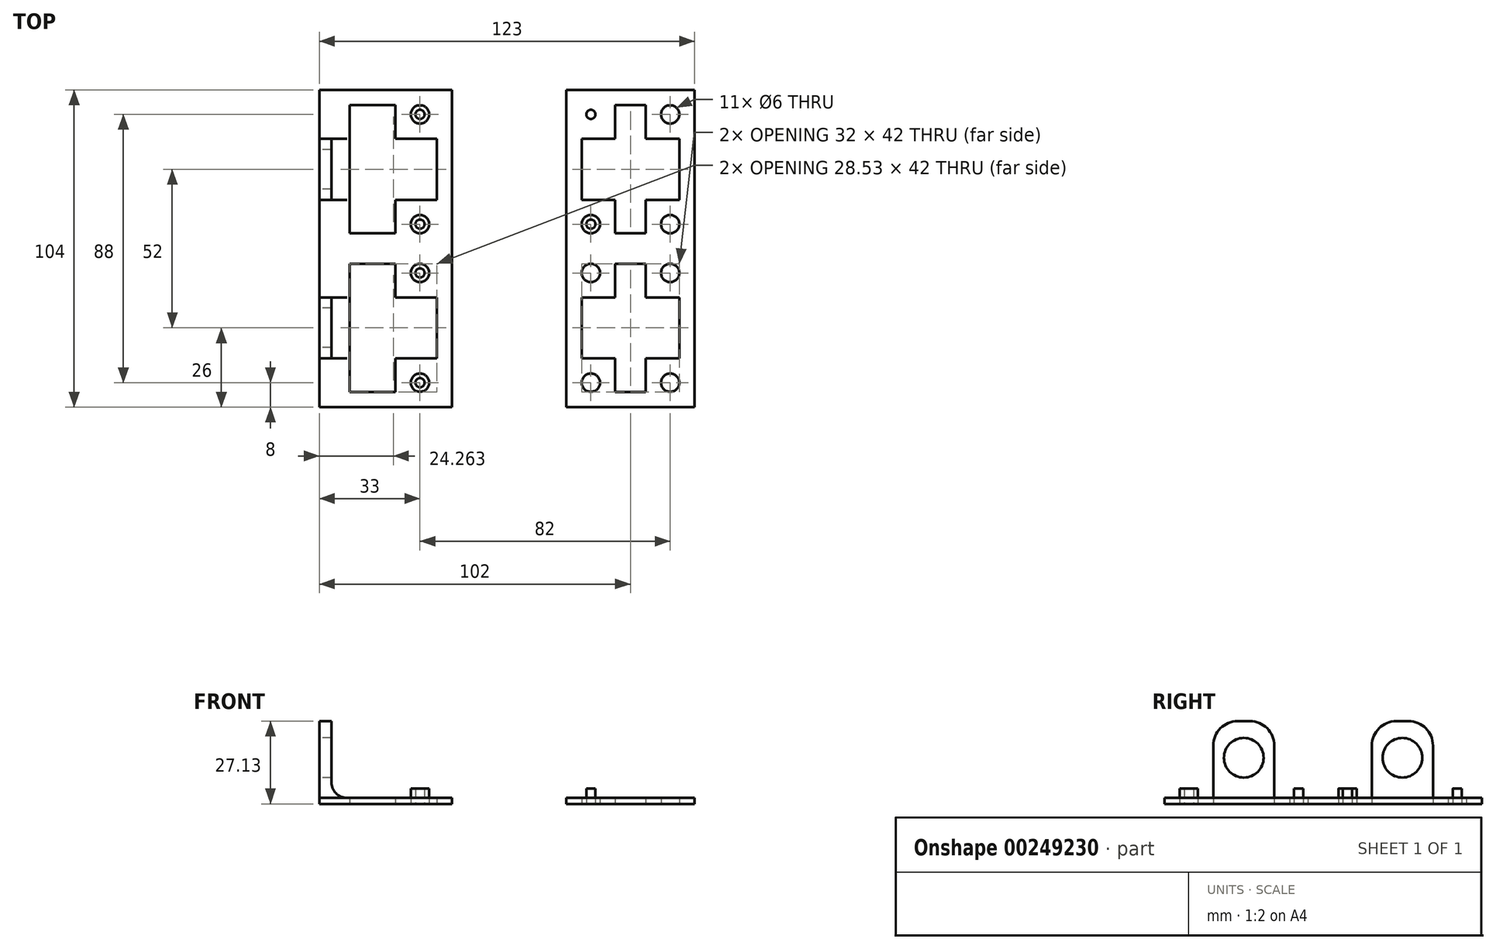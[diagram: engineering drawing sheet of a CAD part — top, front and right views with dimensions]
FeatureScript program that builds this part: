
annotation { "Feature Type Name" : "Feature", "Feature Type Description" : "" }
export const myFeature = defineFeature(function(context is Context, id is Id, definition is map)
    precondition{}
    {
        {
            var Q0;
            Q0=qCreatedBy(makeId("Top.planeOp"),FACE);
            var sketch = newSketch(context, id + "F0", { "sketchPlane" : qUnion([Q0])});
            skLineSegment(sketch, "E0.bottom", {"start": v(-10, 5) * mm, "end": v(-72, 5) * mm, "construction": true});
            skLineSegment(sketch, "E0.top", {"start": v(-10, 47) * mm, "end": v(-72, 47) * mm, "construction": true});
            skLineSegment(sketch, "E0.left", {"start": v(-10, 5) * mm, "end": v(-10, 47) * mm, "construction": true});
            skLineSegment(sketch, "E0.right", {"start": v(-72, 5) * mm, "end": v(-72, 47) * mm, "construction": true});
            skCircle(sketch, "E1", {"center": v(-13, 44) * mm, "radius": 1.5 * mm});
            skLineSegment(sketch, "E2", {"start": v(-41, 47) * mm, "end": v(-41, 5) * mm, "construction": true});
            skLineSegment(sketch, "E3", {"start": v(-72, 26) * mm, "end": v(-10, 26) * mm, "construction": true});
            skCircle(sketch, "E4.MirrorC", {"center": v(-13, 8) * mm, "radius": 1.5 * mm});
            skCircle(sketch, "E5.MirrorC", {"center": v(-69, 44) * mm, "radius": 1.5 * mm});
            skCircle(sketch, "E6.MirrorC", {"center": v(-69, 8) * mm, "radius": 1.5 * mm});
            skLineSegment(sketch, "E7", {"start": v(-102, -52) * mm, "end": v(-14, -52) * mm, "construction": true});
            skLineSegment(sketch, "E8", {"start": v(-102, 52) * mm, "end": v(-102, -52) * mm, "construction": true});
            skLineSegment(sketch, "E9", {"start": v(122, -62) * mm, "end": v(122, 62) * mm, "construction": true});
            skLineSegment(sketch, "E10.bottom", {"start": v(-102, 52) * mm, "end": v(-58.47, 52) * mm});
            skLineSegment(sketch, "E10.top", {"start": v(-102, -52) * mm, "end": v(-48, -52) * mm});
            skLineSegment(sketch, "E10.left", {"start": v(-102, 52) * mm, "end": v(-102, -52) * mm});
            skCircle(sketch, "E11", {"center": v(-13, 44) * mm, "radius": 3 * mm});
            skCircle(sketch, "E12.MirrorC", {"center": v(-13, 8) * mm, "radius": 3 * mm});
            skCircle(sketch, "E13.MirrorC", {"center": v(-69, 44) * mm, "radius": 3 * mm});
            skCircle(sketch, "E14.MirrorC", {"center": v(-69, 8) * mm, "radius": 3 * mm});
            skLineSegment(sketch, "E15", {"start": v(-58.47, 52) * mm, "end": v(-58.47, -52) * mm});
            skPoint(sketch, "E16.MirrorCS.end.orphan", {"position": v(102, -52) * mm});
            skPoint(sketch, "E16.MirrorCS.start.orphan", {"position": v(102, 52) * mm});
            skPoint(sketch, "E17.trimOffspring.end.orphan", {"position": v(48, -52) * mm});
            skLineSegment(sketch, "E18.MirrorCS", {"start": v(20, 52) * mm, "end": v(-23.53, 52) * mm});
            skLineSegment(sketch, "E19.MirrorCS", {"start": v(20, -52) * mm, "end": v(-68, -52) * mm, "construction": true});
            skLineSegment(sketch, "E20.bottom", {"start": v(-23.53, 52) * mm, "end": v(20, 52) * mm});
            skLineSegment(sketch, "E20.top", {"start": v(-24.76, -52) * mm, "end": v(20, -52) * mm});
            skCircle(sketch, "E21.MirrorC", {"center": v(13, 44) * mm, "radius": 3 * mm});
            skCircle(sketch, "E22.MirrorC", {"center": v(13, 44) * mm, "radius": 1.5 * mm});
            skCircle(sketch, "E23.MirrorC", {"center": v(13, 8) * mm, "radius": 3 * mm});
            skCircle(sketch, "E24.MirrorC", {"center": v(13, 8) * mm, "radius": 1.5 * mm});
            skLineSegment(sketch, "E25.MirrorCS", {"start": v(72, 5) * mm, "end": v(72, 47) * mm, "construction": true});
            skLineSegment(sketch, "E26.MirrorCS", {"start": v(10, 5) * mm, "end": v(10, 47) * mm, "construction": true});
            skLineSegment(sketch, "E27.MirrorCS", {"start": v(10, 5) * mm, "end": v(72, 5) * mm, "construction": true});
            skLineSegment(sketch, "E28.MirrorCS", {"start": v(10, 47) * mm, "end": v(72, 47) * mm, "construction": true});
            skLineSegment(sketch, "E29.bottom", {"start": v(-77, 47) * mm, "end": v(-92, 47) * mm});
            skLineSegment(sketch, "E29.top", {"start": v(-77, 5) * mm, "end": v(-92, 5) * mm});
            skLineSegment(sketch, "E29.left", {"start": v(-77, 47) * mm, "end": v(-77, 5) * mm});
            skLineSegment(sketch, "E29.right", {"start": v(-92, 47) * mm, "end": v(-92, 5) * mm});
            skLineSegment(sketch, "E30.bottom", {"start": v(-5, 47) * mm, "end": v(5, 47) * mm});
            skLineSegment(sketch, "E30.top", {"start": v(-5, 5) * mm, "end": v(5, 5) * mm});
            skLineSegment(sketch, "E30.left", {"start": v(-5, 47) * mm, "end": v(-5, 5) * mm});
            skLineSegment(sketch, "E30.right", {"start": v(5, 47) * mm, "end": v(5, 5) * mm});
            skCircle(sketch, "E31.MirrorC", {"center": v(-69, -8) * mm, "radius": 1.5 * mm});
            skCircle(sketch, "E32.MirrorC", {"center": v(-69, -8) * mm, "radius": 3 * mm});
            skCircle(sketch, "E33.MirrorC", {"center": v(-13, -8) * mm, "radius": 3 * mm});
            skCircle(sketch, "E34.MirrorC", {"center": v(-13, -8) * mm, "radius": 1.5 * mm});
            skCircle(sketch, "E35.MirrorC", {"center": v(13, -8) * mm, "radius": 3 * mm});
            skCircle(sketch, "E36.MirrorC", {"center": v(13, -8) * mm, "radius": 1.5 * mm});
            skCircle(sketch, "E37.MirrorC", {"center": v(13, -44) * mm, "radius": 3 * mm});
            skCircle(sketch, "E38.MirrorC", {"center": v(13, -44) * mm, "radius": 1.5 * mm});
            skCircle(sketch, "E39.MirrorC", {"center": v(-13, -44) * mm, "radius": 3 * mm});
            skCircle(sketch, "E40.MirrorC", {"center": v(-13, -44) * mm, "radius": 1.5 * mm});
            skCircle(sketch, "E41.MirrorC", {"center": v(-69, -44) * mm, "radius": 3 * mm});
            skCircle(sketch, "E42.MirrorC", {"center": v(-69, -44) * mm, "radius": 1.5 * mm});
            skLineSegment(sketch, "E43.MirrorCS", {"start": v(-10, -5) * mm, "end": v(-72, -5) * mm, "construction": true});
            skLineSegment(sketch, "E44.MirrorCS", {"start": v(-10, -47) * mm, "end": v(-72, -47) * mm, "construction": true});
            skLineSegment(sketch, "E45.MirrorCS", {"start": v(-72, -5) * mm, "end": v(-72, -47) * mm, "construction": true});
            skLineSegment(sketch, "E46.MirrorCS", {"start": v(-10, -5) * mm, "end": v(-10, -47) * mm, "construction": true});
            skLineSegment(sketch, "E47.MirrorCS", {"start": v(10, -5) * mm, "end": v(10, -47) * mm, "construction": true});
            skLineSegment(sketch, "E48.MirrorCS", {"start": v(10, -5) * mm, "end": v(72, -5) * mm, "construction": true});
            skLineSegment(sketch, "E49.MirrorCS", {"start": v(10, -47) * mm, "end": v(72, -47) * mm, "construction": true});
            skLineSegment(sketch, "E50.MirrorCS", {"start": v(72, -5) * mm, "end": v(72, -47) * mm, "construction": true});
            skLineSegment(sketch, "E51.MirrorCS", {"start": v(-92, -47) * mm, "end": v(-92, -5) * mm});
            skLineSegment(sketch, "E52.MirrorCS", {"start": v(-77, -47) * mm, "end": v(-92, -47) * mm});
            skLineSegment(sketch, "E53.MirrorCS", {"start": v(-77, -47) * mm, "end": v(-77, -5) * mm});
            skLineSegment(sketch, "E54.MirrorCS", {"start": v(-77, -5) * mm, "end": v(-92, -5) * mm});
            skLineSegment(sketch, "E55.MirrorCS", {"start": v(-5, -5) * mm, "end": v(5, -5) * mm});
            skLineSegment(sketch, "E56.MirrorCS", {"start": v(5, -47) * mm, "end": v(5, -5) * mm});
            skLineSegment(sketch, "E57.MirrorCS", {"start": v(-5, -47) * mm, "end": v(-5, -5) * mm});
            skLineSegment(sketch, "E58.MirrorCS", {"start": v(-5, -47) * mm, "end": v(5, -47) * mm});
            skLineSegment(sketch, "E59.bottom", {"start": v(-80.53, 36) * mm, "end": v(-63.47, 36) * mm});
            skLineSegment(sketch, "E59.top", {"start": v(-80.53, 16) * mm, "end": v(-63.47, 16) * mm});
            skLineSegment(sketch, "E59.left", {"start": v(-80.53, 36) * mm, "end": v(-80.53, 16) * mm});
            skLineSegment(sketch, "E59.right", {"start": v(-63.47, 36) * mm, "end": v(-63.47, 16) * mm});
            skPoint(sketch, "E59.middle", {"position": v(-72, 26) * mm});
            skLineSegment(sketch, "E60.MirrorCS", {"start": v(-63.47, -36) * mm, "end": v(-63.47, -16) * mm});
            skLineSegment(sketch, "E61.MirrorCS", {"start": v(-80.53, -16) * mm, "end": v(-63.47, -16) * mm});
            skLineSegment(sketch, "E62.MirrorCS", {"start": v(-80.53, -36) * mm, "end": v(-80.53, -16) * mm});
            skLineSegment(sketch, "E63.MirrorCS", {"start": v(-80.53, -36) * mm, "end": v(-63.47, -36) * mm});
            skLineSegment(sketch, "E64", {"start": v(-10, 26) * mm, "end": v(10, 26) * mm, "construction": true});
            skLineSegment(sketch, "E65", {"start": v(0, 47) * mm, "end": v(0, 5) * mm, "construction": true});
            skLineSegment(sketch, "E66.bottom", {"start": v(-16, 36) * mm, "end": v(16, 36) * mm});
            skLineSegment(sketch, "E66.top", {"start": v(-16, 16) * mm, "end": v(16, 16) * mm});
            skLineSegment(sketch, "E66.left", {"start": v(-16, 36) * mm, "end": v(-16, 16) * mm});
            skLineSegment(sketch, "E66.right", {"start": v(16, 36) * mm, "end": v(16, 16) * mm});
            skPoint(sketch, "E66.middle", {"position": v(0, 26) * mm});
            skLineSegment(sketch, "E67.bottom", {"start": v(20, 52) * mm, "end": v(-20, 52) * mm});
            skLineSegment(sketch, "E67.top", {"start": v(20, -52) * mm, "end": v(-20, -52) * mm});
            skPoint(sketch, "E67.middle", {"position": v(0, 0) * mm});
            skPoint(sketch, "E68.trimOffspring.end.orphan", {"position": v(-23.53, -52) * mm});
            skLineSegment(sketch, "E69.bottom", {"start": v(21, 52) * mm, "end": v(-21, 52) * mm});
            skLineSegment(sketch, "E69.top", {"start": v(21, -52) * mm, "end": v(-21, -52) * mm});
            skLineSegment(sketch, "E69.left", {"start": v(21, 52) * mm, "end": v(21, -52) * mm});
            skLineSegment(sketch, "E69.right", {"start": v(-21, 52) * mm, "end": v(-21, -52) * mm});
            skLineSegment(sketch, "E70.MirrorCS", {"start": v(16, -36) * mm, "end": v(16, -16) * mm});
            skLineSegment(sketch, "E71.MirrorCS", {"start": v(-16, -36) * mm, "end": v(16, -36) * mm});
            skLineSegment(sketch, "E72.MirrorCS", {"start": v(-16, -36) * mm, "end": v(-16, -16) * mm});
            skLineSegment(sketch, "E73.MirrorCS", {"start": v(-16, -16) * mm, "end": v(16, -16) * mm});
            skSolve(sketch);
        }
        {
            var Q0;
            Q0=makeQuery(id+"F0.imprint","IMPRINT",FACE,{"disambiguationData":[TD([[makeQuery(id+"F0.imprint","IMPRINT",EDGE,{"derivedFrom":sQuery(id+"F0.wireOp",EDGE,"E4.MirrorC")}),1.0]])]});
            var Q1;
            Q1=makeQuery(id+"F0.imprint","IMPRINT",FACE,{"disambiguationData":[TD([[makeQuery(id+"F0.imprint","IMPRINT",EDGE,{"derivedFrom":sQuery(id+"F0.wireOp",EDGE,"E10.bottom")}),-1.0]])]});
            var Q2;
            Q2=makeQuery(id+"F0.imprint","IMPRINT",FACE,{"disambiguationData":[TD([[makeQuery(id+"F0.imprint","IMPRINT",EDGE,{"derivedFrom":sQuery(id+"F0.wireOp",EDGE,"E1")}),-1.0]])]});
            var Q3;
            Q3=makeQuery(id+"F0.imprint","IMPRINT",FACE,{"disambiguationData":[TD([[makeQuery(id+"F0.imprint","IMPRINT",EDGE,{"derivedFrom":sQuery(id+"F0.wireOp",EDGE,"E4.MirrorC")}),1.0]])]});
            var Q4;
            Q4=makeQuery(id+"F0.imprint","IMPRINT",FACE,{"disambiguationData":[TD([[makeQuery(id+"F0.imprint","IMPRINT",EDGE,{"derivedFrom":sQuery(id+"F0.wireOp",EDGE,"E11")}),-1.0]])]});
            extrude(context, id + "F1", {"entities" : qUnion([Q0, Q1, Q2, Q3, Q4]), "depth" : 2 * mm});
        }
        {
            var Q0;
            Q0=makeQuery(id+"F0.imprint","IMPRINT",FACE,{"disambiguationData":[TD([[makeQuery(id+"F0.imprint","IMPRINT",EDGE,{"derivedFrom":sQuery(id+"F0.wireOp",EDGE,"E5.MirrorC")}),1.0]])]});
            var Q1;
            Q1=makeQuery(id+"F0.imprint","IMPRINT",FACE,{"disambiguationData":[TD([[makeQuery(id+"F0.imprint","IMPRINT",EDGE,{"derivedFrom":sQuery(id+"F0.wireOp",EDGE,"E6.MirrorC")}),-1.0]])]});
            var Q2;
            Q2=makeQuery(id+"F0.imprint","IMPRINT",FACE,{"disambiguationData":[TD([[makeQuery(id+"F0.imprint","IMPRINT",EDGE,{"derivedFrom":sQuery(id+"F0.wireOp",EDGE,"E4.MirrorC")}),1.0]])]});
            var Q3;
            Q3=makeQuery(id+"F0.imprint","IMPRINT",FACE,{"disambiguationData":[TD([[makeQuery(id+"F0.imprint","IMPRINT",EDGE,{"derivedFrom":sQuery(id+"F0.wireOp",EDGE,"E1")}),-1.0]])]});
            var Q4;
            Q4=makeQuery(id+"F0.imprint","IMPRINT",FACE,{"disambiguationData":[TD([[makeQuery(id+"F0.imprint","IMPRINT",EDGE,{"derivedFrom":sQuery(id+"F0.wireOp",EDGE,"54afa595-782a-44cc-b530-174a9ed369d55.MirrorC")}),1.0]])]});
            var Q5;
            Q5=makeQuery(id+"F0.imprint","IMPRINT",FACE,{"disambiguationData":[TD([[makeQuery(id+"F0.imprint","IMPRINT",EDGE,{"derivedFrom":sQuery(id+"F0.wireOp",EDGE,"54afa595-782a-44cc-b530-174a9ed369d57.MirrorC")}),-1.0]])]});
            var Q6;
            Q6=makeQuery(id+"F0.imprint","IMPRINT",FACE,{"disambiguationData":[TD([[makeQuery(id+"F0.imprint","IMPRINT",EDGE,{"derivedFrom":sQuery(id+"F0.wireOp",EDGE,"25e94151-ceff-47d8-9de0-a60d4fc2466f5.MirrorC")}),1.0]])]});
            var Q7;
            Q7=makeQuery(id+"F0.imprint","IMPRINT",FACE,{"disambiguationData":[TD([[makeQuery(id+"F0.imprint","IMPRINT",EDGE,{"derivedFrom":sQuery(id+"F0.wireOp",EDGE,"25e94151-ceff-47d8-9de0-a60d4fc2466f7.MirrorC")}),-1.0]])]});
            var Q8;
            Q8=makeQuery(id+"F0.imprint","IMPRINT",FACE,{"disambiguationData":[TD([[makeQuery(id+"F0.imprint","IMPRINT",EDGE,{"derivedFrom":sQuery(id+"F0.wireOp",EDGE,"54afa595-782a-44cc-b530-174a9ed369d59.MirrorC")}),-1.0]])]});
            var Q9;
            Q9=makeQuery(id+"F0.imprint","IMPRINT",FACE,{"disambiguationData":[TD([[makeQuery(id+"F0.imprint","IMPRINT",EDGE,{"derivedFrom":sQuery(id+"F0.wireOp",EDGE,"25e94151-ceff-47d8-9de0-a60d4fc2466f19.MirrorC")}),1.0]])]});
            var Q10;
            Q10=makeQuery(id+"F0.imprint","IMPRINT",FACE,{"disambiguationData":[TD([[makeQuery(id+"F0.imprint","IMPRINT",EDGE,{"derivedFrom":sQuery(id+"F0.wireOp",EDGE,"25e94151-ceff-47d8-9de0-a60d4fc2466f14.MirrorC")}),-1.0]])]});
            var Q11;
            Q11=makeQuery(id+"F0.imprint","IMPRINT",FACE,{"disambiguationData":[TD([[makeQuery(id+"F0.imprint","IMPRINT",EDGE,{"derivedFrom":sQuery(id+"F0.wireOp",EDGE,"25e94151-ceff-47d8-9de0-a60d4fc2466f6.MirrorC")}),-1.0]])]});
            var Q12;
            Q12=makeQuery(id+"F0.imprint","IMPRINT",FACE,{"disambiguationData":[TD([[makeQuery(id+"F0.imprint","IMPRINT",EDGE,{"derivedFrom":sQuery(id+"F0.wireOp",EDGE,"25e94151-ceff-47d8-9de0-a60d4fc2466f11.MirrorC")}),1.0]])]});
            var Q13;
            Q13=makeQuery(id+"F0.imprint","IMPRINT",FACE,{"disambiguationData":[TD([[makeQuery(id+"F0.imprint","IMPRINT",EDGE,{"derivedFrom":sQuery(id+"F0.wireOp",EDGE,"25e94151-ceff-47d8-9de0-a60d4fc2466f16.MirrorC")}),1.0]])]});
            var Q14;
            Q14=makeQuery(id+"F0.imprint","IMPRINT",FACE,{"disambiguationData":[TD([[makeQuery(id+"F0.imprint","IMPRINT",EDGE,{"derivedFrom":sQuery(id+"F0.wireOp",EDGE,"54afa595-782a-44cc-b530-174a9ed369d53.MirrorC")}),1.0]])]});
            var Q15;
            Q15=makeQuery(id+"F0.imprint","IMPRINT",FACE,{"disambiguationData":[TD([[makeQuery(id+"F0.imprint","IMPRINT",EDGE,{"derivedFrom":sQuery(id+"F0.wireOp",EDGE,"25e94151-ceff-47d8-9de0-a60d4fc2466f17.MirrorC")}),-1.0]])]});
            var Q16;
            Q16=makeQuery(id+"F0.imprint","IMPRINT",FACE,{"disambiguationData":[TD([[makeQuery(id+"F0.imprint","IMPRINT",EDGE,{"derivedFrom":sQuery(id+"F0.wireOp",EDGE,"E21.MirrorC")}),-1.0]])]});
            var Q17;
            Q17=makeQuery(id+"F0.imprint","IMPRINT",FACE,{"disambiguationData":[TD([[makeQuery(id+"F0.imprint","IMPRINT",EDGE,{"derivedFrom":sQuery(id+"F0.wireOp",EDGE,"E23.MirrorC")}),1.0]])]});
            var Q18;
            Q18=makeQuery(id+"F0.imprint","IMPRINT",FACE,{"disambiguationData":[TD([[makeQuery(id+"F0.imprint","IMPRINT",EDGE,{"derivedFrom":sQuery(id+"F0.wireOp",EDGE,"E31.MirrorC")}),1.0]])]});
            var Q19;
            Q19=makeQuery(id+"F0.imprint","IMPRINT",FACE,{"disambiguationData":[TD([[makeQuery(id+"F0.imprint","IMPRINT",EDGE,{"derivedFrom":sQuery(id+"F0.wireOp",EDGE,"E33.MirrorC")}),1.0]])]});
            var Q20;
            Q20=makeQuery(id+"F0.imprint","IMPRINT",FACE,{"disambiguationData":[TD([[makeQuery(id+"F0.imprint","IMPRINT",EDGE,{"derivedFrom":sQuery(id+"F0.wireOp",EDGE,"E35.MirrorC")}),-1.0]])]});
            var Q21;
            Q21=makeQuery(id+"F0.imprint","IMPRINT",FACE,{"disambiguationData":[TD([[makeQuery(id+"F0.imprint","IMPRINT",EDGE,{"derivedFrom":sQuery(id+"F0.wireOp",EDGE,"E41.MirrorC")}),1.0]])]});
            var Q22;
            Q22=makeQuery(id+"F0.imprint","IMPRINT",FACE,{"disambiguationData":[TD([[makeQuery(id+"F0.imprint","IMPRINT",EDGE,{"derivedFrom":sQuery(id+"F0.wireOp",EDGE,"E39.MirrorC")}),-1.0]])]});
            var Q23;
            Q23=makeQuery(id+"F0.imprint","IMPRINT",FACE,{"disambiguationData":[TD([[makeQuery(id+"F0.imprint","IMPRINT",EDGE,{"derivedFrom":sQuery(id+"F0.wireOp",EDGE,"E37.MirrorC")}),1.0]])]});
            extrude(context, id + "F2", {"entities" : qUnion([Q0, Q1, Q2, Q3, Q4, Q5, Q6, Q7, Q8, Q9, Q10, Q11, Q12, Q13, Q14, Q15, Q16, Q17, Q18, Q19, Q20, Q21, Q22, Q23]), "depth" : 5 * mm});
        }
        {
            var Q0;
            Q0=qCreatedBy(makeId("Right.planeOp"),FACE);
            var sketch = newSketch(context, id + "F3", { "sketchPlane" : qUnion([Q0])});
            skLineSegment(sketch, "E74.0", {"start": v(52, 2) * mm, "end": v(52, 0) * mm, "construction": true});
            skLineSegment(sketch, "E75.0", {"start": v(52, 0) * mm, "end": v(37.33, 0) * mm, "construction": true});
            skPoint(sketch, "E76.0", {"position": v(0, 0) * mm});
            skLineSegment(sketch, "E77", {"start": v(0, 0) * mm, "end": v(0, 14.94) * mm, "construction": true});
            skLineSegment(sketch, "E78.bottom", {"start": v(31, 0) * mm, "end": v(37.33, 0) * mm});
            skLineSegment(sketch, "E79", {"start": v(36, 28.6) * mm, "end": v(19, 0) * mm, "construction": true});
            skLineSegment(sketch, "E80", {"start": v(14.66, 30.25) * mm, "end": v(37.33, 0) * mm, "construction": true});
            skCircle(sketch, "E81", {"center": v(26, 15.13) * mm, "radius": 6.5 * mm});
            skPoint(sketch, "E82.MirrorCS.start.orphan", {"position": v(31, 30) * mm});
            skPoint(sketch, "E83.MirrorCS.end.orphan", {"position": v(19, 30) * mm});
            skLineSegment(sketch, "E84.trimOffspring", {"start": v(19, 0) * mm, "end": v(-52, 0) * mm, "construction": true});
            skLineSegment(sketch, "E85.bottom", {"start": v(36, 0) * mm, "end": v(16, 0.47) * mm});
            skLineSegment(sketch, "E85.left", {"start": v(36, 0) * mm, "end": v(36, 27.13) * mm});
            skLineSegment(sketch, "E85.right", {"start": v(16, 0.47) * mm, "end": v(16, 28.47) * mm});
            skLineSegment(sketch, "E86", {"start": v(36, 27.13) * mm, "end": v(16, 27.13) * mm});
            skPoint(sketch, "E87.orphan", {"position": v(36, 29.78) * mm});
            skPoint(sketch, "E88.orphan", {"position": v(16, 30.25) * mm});
            skCircle(sketch, "E89.MirrorC", {"center": v(-26, 15.13) * mm, "radius": 6.5 * mm});
            skLineSegment(sketch, "E90.MirrorCS", {"start": v(-36, 27.13) * mm, "end": v(-16, 27.13) * mm});
            skLineSegment(sketch, "E91.MirrorCS", {"start": v(-16, 0.47) * mm, "end": v(-16, 28.47) * mm});
            skLineSegment(sketch, "E92.MirrorCS", {"start": v(-36, 0) * mm, "end": v(-36, 27.13) * mm});
            skLineSegment(sketch, "E93.MirrorCS", {"start": v(-36, 0) * mm, "end": v(-16, 0.47) * mm});
            skLineSegment(sketch, "E94", {"start": v(41, 0) * mm, "end": v(41, 5) * mm});
            skLineSegment(sketch, "E95", {"start": v(11, 5) * mm, "end": v(11, 0) * mm});
            skSolve(sketch);
        }
        {
            var Q0;
            Q0=makeQuery(id+"F1.opExtrude","SWEPT_FACE",FACE,{"disambiguationData":[OSD([sQuery(id+"F0.wireOp",EDGE,"E10.left")])]});
            var sketch = newSketch(context, id + "F4", { "sketchPlane" : qUnion([Q0])});
            skCircle(sketch, "E96.0", {"center": v(-26, 15.13) * mm, "radius": 6.5 * mm});
            skLineSegment(sketch, "E97.0", {"start": v(-36, 27.13) * mm, "end": v(-16, 27.13) * mm});
            skLineSegment(sketch, "E98.0", {"start": v(-16, 0.47) * mm, "end": v(-16, 28.47) * mm});
            skLineSegment(sketch, "E99.0", {"start": v(-36, 0) * mm, "end": v(-36, 27.13) * mm});
            skLineSegment(sketch, "E100.0.0", {"start": v(-16, 0.47) * mm, "end": v(-36, 0) * mm});
            skLineSegment(sketch, "E100.0.3", {"start": v(-16, 27.13) * mm, "end": v(-16, 0.47) * mm});
            skLineSegment(sketch, "E101.0.0", {"start": v(36, 0) * mm, "end": v(16, 0.47) * mm});
            skLineSegment(sketch, "E101.0.1", {"start": v(16, 0.47) * mm, "end": v(16, 27.13) * mm});
            skLineSegment(sketch, "E101.0.2", {"start": v(16, 27.13) * mm, "end": v(36, 27.13) * mm});
            skLineSegment(sketch, "E101.0.3", {"start": v(36, 27.13) * mm, "end": v(36, 0) * mm});
            skCircle(sketch, "E102.0", {"center": v(26, 15.13) * mm, "radius": 6.5 * mm});
            skSolve(sketch);
        }
        {
            var Q0;
            Q0=qSketchRegion(id+"F4",true);
            extrude(context, id + "F5", {"entities" : qUnion([Q0]), "operationType" : NewBodyOperationType.ADD, "oppositeDirection" : true, "depth" : 4 * mm});
        }
        {
            var Q0;
            Q0=makeQuery(id+"F5.boolean.opBoolean","INTERSECT",EDGE,{"derivedFrom":[makeQuery(id+"F1.opExtrude","CAP_FACE",FACE,{"disambiguationData":[OSD([sQuery(id+"F0.wireOp",EDGE,"E10.bottom"),sQuery(id+"F0.wireOp",EDGE,"E10.top"),sQuery(id+"F0.wireOp",EDGE,"E10.left"),sQuery(id+"F0.wireOp",EDGE,"E13.MirrorC"),sQuery(id+"F0.wireOp",EDGE,"E14.MirrorC"),sQuery(id+"F0.wireOp",EDGE,"E15")])],"isStart":false}),makeQuery(id+"F5.opExtrude","CAP_FACE",FACE,{"disambiguationData":[OSD([sQuery(id+"F4.wireOp",EDGE,"E96.0"),sQuery(id+"F4.wireOp",EDGE,"E100.0.0"),sQuery(id+"F4.wireOp",EDGE,"E99.0"),sQuery(id+"F4.wireOp",EDGE,"E97.0"),sQuery(id+"F4.wireOp",EDGE,"E100.0.3")])],"isStart":false})]});
            var Q1;
            Q1=makeQuery(id+"F5.boolean.opBoolean","INTERSECT",EDGE,{"derivedFrom":[makeQuery(id+"F1.opExtrude","CAP_FACE",FACE,{"disambiguationData":[OSD([sQuery(id+"F0.wireOp",EDGE,"E10.bottom"),sQuery(id+"F0.wireOp",EDGE,"E10.top"),sQuery(id+"F0.wireOp",EDGE,"E10.left"),sQuery(id+"F0.wireOp",EDGE,"E13.MirrorC"),sQuery(id+"F0.wireOp",EDGE,"E14.MirrorC"),sQuery(id+"F0.wireOp",EDGE,"E15")])],"isStart":false}),makeQuery(id+"F5.opExtrude","CAP_FACE",FACE,{"disambiguationData":[OSD([sQuery(id+"F4.wireOp",EDGE,"E101.0.0"),sQuery(id+"F4.wireOp",EDGE,"E101.0.1"),sQuery(id+"F4.wireOp",EDGE,"E101.0.2"),sQuery(id+"F4.wireOp",EDGE,"E101.0.3"),sQuery(id+"F4.wireOp",EDGE,"E102.0")])],"isStart":false})]});
            fillet(context, id + "F6", {"entities" : qUnion([Q0, Q1]), "radius" : 5 * mm, "tangentPropagation" : true, "allowEdgeOverflow" : false});
        }
        {
            var Q0;
            Q0=makeQuery(id+"F5.opExtrude","SWEPT_EDGE",EDGE,{"disambiguationData":[OSD([sQuery(id+"F4.wireOp",EDGE,"E99.0"),sQuery(id+"F4.wireOp",EDGE,"E97.0")])]});
            var Q1;
            Q1=makeQuery(id+"F5.opExtrude","SWEPT_EDGE",EDGE,{"disambiguationData":[OSD([sQuery(id+"F4.wireOp",EDGE,"E101.0.1"),sQuery(id+"F4.wireOp",EDGE,"E101.0.2")])]});
            var Q2;
            Q2=makeQuery(id+"F5.opExtrude","SWEPT_EDGE",EDGE,{"disambiguationData":[OSD([sQuery(id+"F4.wireOp",EDGE,"E97.0"),sQuery(id+"F4.wireOp",EDGE,"E100.0.3")])]});
            var Q3;
            Q3=makeQuery(id+"F5.opExtrude","SWEPT_EDGE",EDGE,{"disambiguationData":[OSD([sQuery(id+"F4.wireOp",EDGE,"E101.0.2"),sQuery(id+"F4.wireOp",EDGE,"E101.0.3")])]});
            fillet(context, id + "F7", {"entities" : qUnion([Q0, Q1, Q2, Q3]), "radius" : 8 * mm, "tangentPropagation" : true, "allowEdgeOverflow" : false});
        }
        {
            var Q0;
            Q0=makeQuery(id+"F2.opExtrude","SWEPT_BODY",BODY,{"disambiguationData":[OSD([sQuery(id+"F0.wireOp",EDGE,"E1"),sQuery(id+"F0.wireOp",EDGE,"E11")])]});
            deleteBodies(context, id + "F8", {"entities" : qUnion([Q0])});
        }
    });
